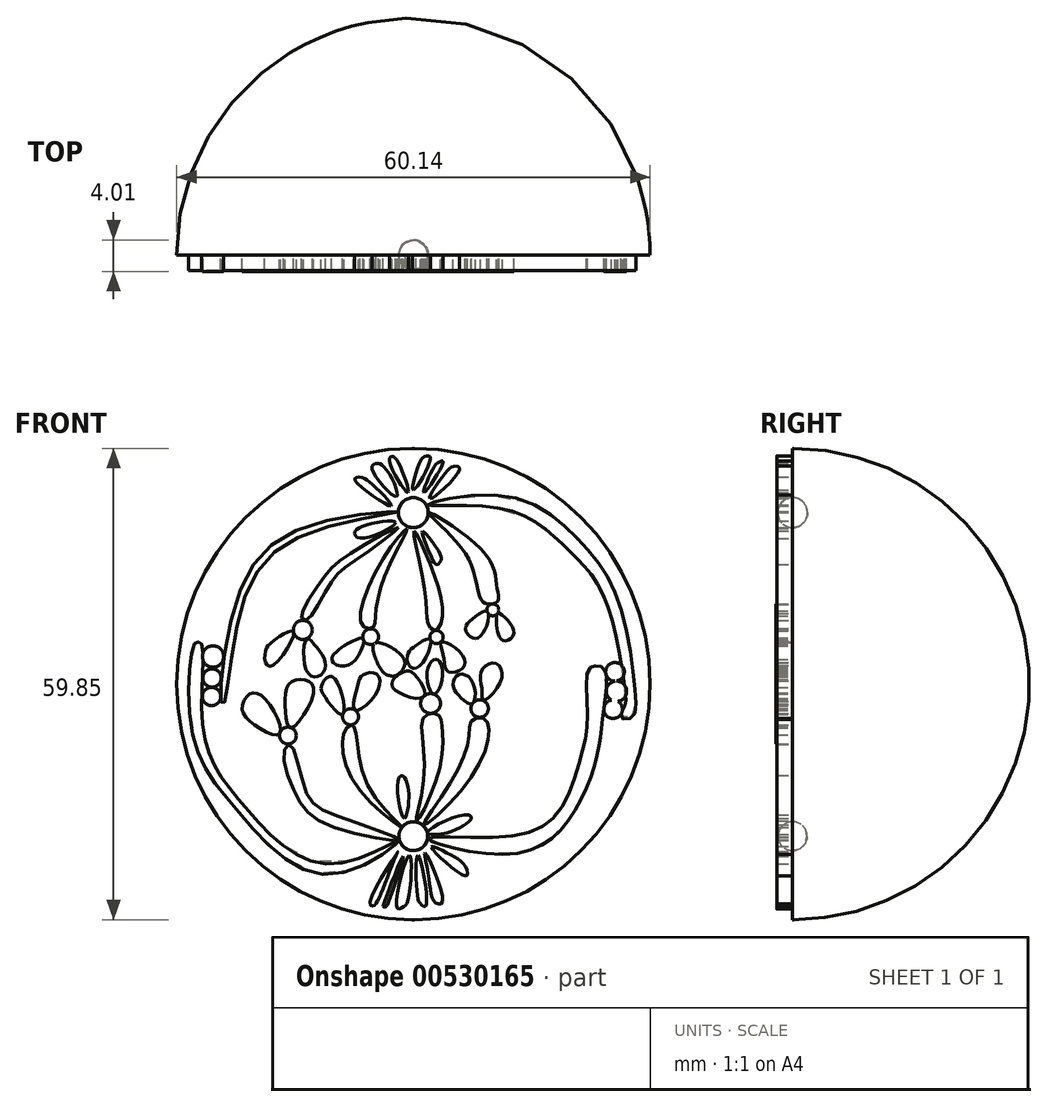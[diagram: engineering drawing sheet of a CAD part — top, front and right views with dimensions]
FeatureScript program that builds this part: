
annotation { "Feature Type Name" : "Feature", "Feature Type Description" : "" }
export const myFeature = defineFeature(function(context is Context, id is Id, definition is map)
    precondition{}
    {
        {
            var Q0;
            Q0=qCreatedBy(makeId("Front.planeOp"),FACE);
            var sketch = newSketch(context, id + "F0", { "sketchPlane" : qUnion([Q0])});
            skArc(sketch, "E0", {"start": v(0, 0) * mm, "mid": v(30.07, 29.93) * mm, "end": v(0, 59.85) * mm});
            skLineSegment(sketch, "E1", {"start": v(0, 0) * mm, "end": v(0, 59.85) * mm});
            skSolve(sketch);
        }
        {
            var Q0;
            Q0 = qSketchRegion(id + "F0", true);
            var Q1;
            Q1=sQuery(id+"F0.wireOp",EDGE,"E1");
            revolve(context, id + "F1", {"entities" : qUnion([Q0]), "axis" : qUnion([Q1]), "revolveType" : RevolveType.ONE_DIRECTION, "angle" : 180 * degree});
        }
        {
            var Q0;
            Q0=makeQuery(id+"F0.imprint","IMPRINT",FACE,{"disambiguationData":[TD([[makeQuery(id+"F0.imprint","IMPRINT",EDGE,{"derivedFrom":sQuery(id+"F0.wireOp",EDGE,"E0")}),1.0]])]});
            var sketch = newSketch(context, id + "F2", { "sketchPlane" : qUnion([Q0])});
            skArc(sketch, "E2", {"start": v(0, 49.81) * mm, "mid": v(1.9, 51.71) * mm, "end": v(0, 53.61) * mm});
            skArc(sketch, "E3", {"start": v(0, 8.77) * mm, "mid": v(1.82, 10.6) * mm, "end": v(0, 12.44) * mm});
            skLineSegment(sketch, "E4", {"start": v(0, 53.61) * mm, "end": v(0, 8.77) * mm});
            skSolve(sketch);
        }
        {
            var Q0;
            Q0 = qSketchRegion(id + "F2", true);
            var Q1;
            Q1=sQuery(id+"F0.wireOp",EDGE,"E1");
            revolve(context, id + "F3", {"entities" : qUnion([Q0]), "axis" : qUnion([Q1]), "revolveType" : RevolveType.FULL});
        }
        {
            var Q0;
            Q0=makeQuery(id+"F0.imprint","IMPRINT",FACE,{"disambiguationData":[TD([[makeQuery(id+"F0.imprint","IMPRINT",EDGE,{"derivedFrom":sQuery(id+"F0.wireOp",EDGE,"E0")}),1.0]])]});
            var sketch = newSketch(context, id + "F4", { "sketchPlane" : qUnion([Q0])});
            skFitSpline(sketch, "E5", {"points": [v(-0.7, 54.26) * mm, v(-3.02, 58.3) * mm, v(-2.66, 58.86) * mm, v(-1.63, 57.5) * mm, v(-0.7, 54.26) * mm]});
            skFitSpline(sketch, "E6", {"points": [v(0, 54.6) * mm, v(0.8, 58.05) * mm, v(1.49, 58.84) * mm, v(2.15, 58.69) * mm, v(0, 54.6) * mm]});
            skFitSpline(sketch, "E7", {"points": [v(1.34, 54.24) * mm, v(2.41, 57.14) * mm, v(3.13, 58.05) * mm, v(3.78, 58.2) * mm, v(1.34, 54.24) * mm]});
            skFitSpline(sketch, "E8", {"points": [v(2.13, 53.49) * mm, v(4.04, 56.7) * mm, v(5.23, 57.61) * mm, v(5.88, 57.23) * mm, v(2.13, 53.49) * mm]});
            skFitSpline(sketch, "E9", {"points": [v(-2.15, 53.73) * mm, v(-3.4, 57.16) * mm, v(-4.76, 57.95) * mm, v(-5.23, 57.27) * mm, v(-2.15, 53.73) * mm]});
            skFitSpline(sketch, "E10", {"points": [v(-2.83, 52.55) * mm, v(-4.86, 54.98) * mm, v(-6.7, 56.18) * mm, v(-7.45, 55.94) * mm, v(-2.83, 52.55) * mm]});
            skFitSpline(sketch, "E11", {"points": [v(-2.25, 50.44) * mm, v(-5.68, 50.24) * mm, v(-7.45, 49.15) * mm, v(-6.63, 48.45) * mm, v(-2.25, 50.44) * mm]});
            skFitSpline(sketch, "E12", {"points": [v(1.15, 49.35) * mm, v(3.26, 46.74) * mm, v(3.52, 45.68) * mm, v(3, 45.11) * mm, v(2.37, 45.92) * mm, v(1.15, 49.35) * mm]});
            skFitSpline(sketch, "E13", {"points": [v(6.93, 51.66) * mm, v(-2.97, 8.5) * mm], "startDerivative": vector(-9.9, -43.15) * mm, "endDerivative": vector(-9.9, -43.15) * mm});
            skSolve(sketch);
        }
        {
            var Q0;
            Q0 = qSketchRegion(id + "F4", true);
            extrude(context, id + "F5", {"entities" : qUnion([Q0]), "depth" : 2 * mm, "offsetDistance" : 25 * mm});
        }
        {
            var Q0;
            Q0=makeQuery(id+"F1.opRevolve","CAP_FACE",FACE,{"disambiguationData":[OSD([sQuery(id+"F0.wireOp",EDGE,"E0"),sQuery(id+"F0.wireOp",EDGE,"E1")])],"isStart":false});
            var sketch = newSketch(context, id + "F6", { "sketchPlane" : qUnion([Q0])});
            skFitSpline(sketch, "E14", {"points": [v(-0.54, 8.19) * mm, v(-0.63, 2.62) * mm, v(-1.32, 1.58) * mm, v(-2.09, 1.52) * mm, v(-0.54, 8.19) * mm]});
            skFitSpline(sketch, "E15", {"points": [v(-1.3, 8.06) * mm, v(-3.12, 2.28) * mm, v(-3.58, 1.59) * mm, v(-3.78, 1.61) * mm, v(-3.7, 2.18) * mm, v(-1.3, 8.06) * mm]});
            skFitSpline(sketch, "E16", {"points": [v(-2.2, 8.15) * mm, v(-3.71, 4.24) * mm, v(-4.63, 2.23) * mm, v(-5.09, 1.75) * mm, v(-5.53, 2.04) * mm, v(-1.96, 8.63) * mm, v(-2.2, 8.15) * mm]});
            skFitSpline(sketch, "E17", {"points": [v(0.6, 8.14) * mm, v(0.47, 3.4) * mm, v(0.94, 2) * mm, v(1.59, 1.78) * mm, v(0.6, 8.14) * mm]});
            skFitSpline(sketch, "E18", {"points": [v(1.5, 8.5) * mm, v(1.97, 5.35) * mm, v(2.66, 2.32) * mm, v(3.66, 2.2) * mm, v(1.5, 8.5) * mm]});
            skFitSpline(sketch, "E19", {"points": [v(2.3, 9.22) * mm, v(4.2, 8.5) * mm, v(6.54, 6.87) * mm, v(6.67, 5.56) * mm, v(2.3, 9.22) * mm]});
            skFitSpline(sketch, "E20", {"points": [v(1.76, 11.07) * mm, v(3.98, 10.98) * mm, v(6.6, 12.13) * mm, v(7.36, 12.94) * mm, v(6.49, 13.32) * mm, v(1.76, 11.07) * mm]});
            skFitSpline(sketch, "E21", {"points": [v(-1.15, 12.88) * mm, v(-0.63, 14.62) * mm, v(-0.7, 16.87) * mm, v(-1.32, 18.28) * mm, v(-1.97, 17.52) * mm, v(-1.15, 12.88) * mm]});
            skSolve(sketch);
        }
        {
            var Q0;
            Q0 = qSketchRegion(id + "F6", true);
            extrude(context, id + "F7", {"entities" : qUnion([Q0]), "depth" : 2 * mm, "offsetDistance" : 25 * mm});
        }
        {
            var Q0;
            Q0=makeQuery(id+"F0.imprint","IMPRINT",FACE,{"disambiguationData":[TD([[makeQuery(id+"F0.imprint","IMPRINT",EDGE,{"derivedFrom":sQuery(id+"F0.wireOp",EDGE,"E0")}),1.0]])]});
            var sketch = newSketch(context, id + "F8", { "sketchPlane" : qUnion([Q0])});
            skFitSpline(sketch, "E22", {"points": [v(-1.98, 51.8) * mm, v(-13.57, 49.94) * mm, v(-22.66, 39.92) * mm, v(-24.32, 27.37) * mm, v(-24.07, 27.46) * mm, v(-21.82, 39.68) * mm, v(-13.27, 49.16) * mm, v(-1.98, 51.8) * mm]});
            skFitSpline(sketch, "E23", {"points": [v(-1.74, 10.12) * mm, v(-10.3, 7.09) * mm, v(-21.48, 14.42) * mm, v(-26.67, 23.9) * mm, v(-26.81, 34.85) * mm, v(-27.25, 35.29) * mm, v(-27.78, 35.05) * mm, v(-28.07, 23.67) * mm, v(-22.28, 13.78) * mm, v(-10.27, 5.73) * mm, v(-1.74, 10.12) * mm]});
            skSolve(sketch);
        }
        {
            var Q0;
            Q0 = qSketchRegion(id + "F8", true);
            extrude(context, id + "F9", {"entities" : qUnion([Q0]), "depth" : 2 * mm, "offsetDistance" : 25 * mm});
        }
        {
            var Q0;
            Q0=makeQuery(id+"F1.opRevolve","CAP_FACE",FACE,{"disambiguationData":[OSD([sQuery(id+"F0.wireOp",EDGE,"E0"),sQuery(id+"F0.wireOp",EDGE,"E1")])],"isStart":false});
            var sketch = newSketch(context, id + "F10", { "sketchPlane" : qUnion([Q0])});
            skPoint(sketch, "E24.0.internal.snap0", {"position": v(-1.9, 51.71) * mm});
            skFitSpline(sketch, "E24", {"points": [v(-1.9, 49.81) * mm, v(-8.07, 46.5) * mm, v(-11.68, 43.09) * mm, v(-14.2, 38.3) * mm, v(-13.52, 38.1) * mm, v(-10.52, 42.73) * mm, v(-7.4, 45.61) * mm, v(-1.9, 49.81) * mm]});
            skFitSpline(sketch, "E25", {"points": [v(-1.76, 10.13) * mm, v(-10.35, 11.84) * mm, v(-14.8, 15.68) * mm, v(-16.41, 21.48) * mm, v(-15.63, 22.2) * mm, v(-13.68, 16.34) * mm, v(-10, 13.29) * mm, v(-1.76, 10.13) * mm]});
            skSolve(sketch);
        }
        {
            var Q0;
            Q0 = qSketchRegion(id + "F10", true);
            extrude(context, id + "F11", {"entities" : qUnion([Q0]), "depth" : 2 * mm, "offsetDistance" : 25 * mm});
        }
        {
            var Q0;
            Q0=makeQuery(id+"F1.opRevolve","CAP_FACE",FACE,{"disambiguationData":[OSD([sQuery(id+"F0.wireOp",EDGE,"E0"),sQuery(id+"F0.wireOp",EDGE,"E1")])],"isStart":false});
            var sketch = newSketch(context, id + "F12", { "sketchPlane" : qUnion([Q0])});
            skFitSpline(sketch, "E26", {"points": [v(-1.43, 11.73) * mm, v(-7.16, 16.9) * mm, v(-8.67, 24.06) * mm, v(-7.65, 24.68) * mm, v(-5.95, 17.42) * mm, v(-1.43, 11.73) * mm]});
            skFitSpline(sketch, "E27", {"points": [v(-0.8, 49.67) * mm, v(-4.32, 45.04) * mm, v(-6.49, 37.4) * mm, v(-5.14, 37.09) * mm, v(-4.83, 38.54) * mm, v(-3.22, 44.64) * mm, v(-0.8, 49.67) * mm]});
            skPoint(sketch, "E28.1.internal.snap0", {"position": v(1.4, 9.45) * mm});
            skPoint(sketch, "E28.2.internal.snap0", {"position": v(1.4, 9.45) * mm});
            skFitSpline(sketch, "E28", {"points": [v(0.4, 12.54) * mm, v(1.4, 18.97) * mm, v(1.4, 25.8) * mm, v(3.17, 26) * mm, v(3.6, 24.89) * mm, v(3.33, 19.16) * mm, v(0.4, 12.54) * mm]});
            skFitSpline(sketch, "E29", {"points": [v(0.07, 49.36) * mm, v(2.33, 44.63) * mm, v(3.7, 38.34) * mm, v(2.77, 36.75) * mm, v(1.9, 37.49) * mm, v(1.56, 41.14) * mm, v(0.07, 49.36) * mm]});
            skSolve(sketch);
        }
        {
            var Q0;
            Q0 = qSketchRegion(id + "F12", true);
            extrude(context, id + "F13", {"entities" : qUnion([Q0]), "depth" : 2 * mm, "offsetDistance" : 25 * mm});
        }
        {
            var Q0;
            Q0=makeQuery(id+"F1.opRevolve","CAP_FACE",FACE,{"disambiguationData":[OSD([sQuery(id+"F0.wireOp",EDGE,"E0"),sQuery(id+"F0.wireOp",EDGE,"E1")])],"isStart":false});
            var sketch = newSketch(context, id + "F14", { "sketchPlane" : qUnion([Q0])});
            skFitSpline(sketch, "E30", {"points": [v(1.9, 51.71) * mm, v(6.97, 45.88) * mm, v(8.88, 40.32) * mm, v(10.67, 40.4) * mm, v(10.64, 42.1) * mm, v(9.2, 46.4) * mm, v(1.9, 51.71) * mm]});
            skFitSpline(sketch, "E31", {"points": [v(1.32, 12.04) * mm, v(4.51, 17.05) * mm, v(7.1, 23.39) * mm, v(7.4, 25.28) * mm, v(9, 25.55) * mm, v(9.6, 23.4) * mm, v(6.1, 16.4) * mm, v(1.32, 12.04) * mm]});
            skSolve(sketch);
        }
        {
            var Q0;
            Q0 = qSketchRegion(id + "F14", true);
            extrude(context, id + "F15", {"entities" : qUnion([Q0]), "depth" : 2 * mm, "offsetDistance" : 25 * mm});
        }
        {
            var Q0;
            Q0=makeQuery(id+"F1.opRevolve","CAP_FACE",FACE,{"disambiguationData":[OSD([sQuery(id+"F0.wireOp",EDGE,"E0"),sQuery(id+"F0.wireOp",EDGE,"E1")])],"isStart":false});
            var sketch = newSketch(context, id + "F16", { "sketchPlane" : qUnion([Q0])});
            skFitSpline(sketch, "E32", {"points": [v(1.85, 52.7) * mm, v(11.43, 53.86) * mm, v(20.84, 48.41) * mm, v(25.86, 40.99) * mm, v(28.2, 28.78) * mm, v(27.73, 25.67) * mm, v(26.41, 25.68) * mm, v(26.81, 27.12) * mm, v(26.94, 28.61) * mm, v(24.44, 40.5) * mm, v(19.62, 47.03) * mm, v(11.21, 52.23) * mm, v(1.85, 52.7) * mm]});
            skFitSpline(sketch, "E33", {"points": [v(1.92, 10.29) * mm, v(11.74, 8.3) * mm, v(19.77, 12.68) * mm, v(23.33, 20.79) * mm, v(24.1, 26.1) * mm, v(24.28, 31.8) * mm, v(23.08, 32.26) * mm, v(22.2, 31.66) * mm, v(22.13, 26) * mm, v(21.35, 20.92) * mm, v(18.4, 13.64) * mm, v(11.44, 10.51) * mm, v(1.92, 10.29) * mm]});
            skSolve(sketch);
        }
        {
            var Q0;
            Q0 = qSketchRegion(id + "F16", true);
            extrude(context, id + "F17", {"entities" : qUnion([Q0]), "depth" : 2 * mm, "offsetDistance" : 25 * mm});
        }
        {
            var Q0;
            Q0=makeQuery(id+"F1.opRevolve","CAP_FACE",FACE,{"disambiguationData":[OSD([sQuery(id+"F0.wireOp",EDGE,"E0"),sQuery(id+"F0.wireOp",EDGE,"E1")])],"isStart":false});
            var sketch = newSketch(context, id + "F18", { "sketchPlane" : qUnion([Q0])});
            skCircle(sketch, "E34", {"center": v(-25.45, 33.43) * mm, "radius": 1.36 * mm});
            skCircle(sketch, "E35", {"center": v(-25.58, 30.7) * mm, "radius": 1.17 * mm});
            skCircle(sketch, "E36", {"center": v(-25.64, 28.35) * mm, "radius": 1.17 * mm});
            skSolve(sketch);
        }
        {
            var Q0;
            Q0 = qSketchRegion(id + "F18", true);
            extrude(context, id + "F19", {"entities" : qUnion([Q0]), "depth" : 2.1 * mm, "offsetDistance" : 25 * mm});
        }
        {
            var Q0;
            Q0=makeQuery(id+"F1.opRevolve","CAP_FACE",FACE,{"disambiguationData":[OSD([sQuery(id+"F0.wireOp",EDGE,"E0"),sQuery(id+"F0.wireOp",EDGE,"E1")])],"isStart":false});
            var sketch = newSketch(context, id + "F20", { "sketchPlane" : qUnion([Q0])});
            skCircle(sketch, "E37", {"center": v(25.38, 26.74) * mm, "radius": 1.18 * mm});
            skCircle(sketch, "E38", {"center": v(25.8, 29.01) * mm, "radius": 1.3 * mm});
            skCircle(sketch, "E39", {"center": v(25.62, 31.48) * mm, "radius": 1.19 * mm});
            skSolve(sketch);
        }
        {
            var Q0;
            Q0 = qSketchRegion(id + "F20", true);
            extrude(context, id + "F21", {"entities" : qUnion([Q0]), "depth" : 2.1 * mm, "offsetDistance" : 25 * mm});
        }
        {
            var Q0;
            {var subQ0=sQuery(id+"F0.wireOp",EDGE,"E0");Q0=makeQuery(id+"F21.boolean.opBoolean","SPLIT",FACE,{"disambiguationData":[TD([makeQuery(id+"F1.opRevolve","SWEPT_FACE",FACE,{"disambiguationData":[OSD([subQ0])]}),makeQuery(id+"F3.opRevolve","SWEPT_FACE",FACE,{"disambiguationData":[OSD([sQuery(id+"F2.wireOp",EDGE,"E2")])]}),makeQuery(id+"F3.opRevolve","SWEPT_FACE",FACE,{"disambiguationData":[OSD([sQuery(id+"F2.wireOp",EDGE,"E3")])]}),makeQuery(id+"F5.opExtrude","SWEPT_FACE",FACE,{"disambiguationData":[OSD([sQuery(id+"F4.wireOp",EDGE,"E5")])]}),makeQuery(id+"F5.opExtrude","SWEPT_FACE",FACE,{"disambiguationData":[OSD([sQuery(id+"F4.wireOp",EDGE,"E6")])]}),makeQuery(id+"F5.opExtrude","SWEPT_FACE",FACE,{"disambiguationData":[OSD([sQuery(id+"F4.wireOp",EDGE,"E7")])]}),makeQuery(id+"F5.opExtrude","SWEPT_FACE",FACE,{"disambiguationData":[OSD([sQuery(id+"F4.wireOp",EDGE,"E8")])]}),makeQuery(id+"F5.opExtrude","SWEPT_FACE",FACE,{"disambiguationData":[OSD([sQuery(id+"F4.wireOp",EDGE,"E9")])]}),makeQuery(id+"F5.opExtrude","SWEPT_FACE",FACE,{"disambiguationData":[OSD([sQuery(id+"F4.wireOp",EDGE,"E10")])]}),makeQuery(id+"F5.opExtrude","SWEPT_FACE",FACE,{"disambiguationData":[OSD([sQuery(id+"F4.wireOp",EDGE,"E11")])]}),makeQuery(id+"F5.opExtrude","SWEPT_FACE",FACE,{"disambiguationData":[OSD([sQuery(id+"F4.wireOp",EDGE,"E12")])]}),makeQuery(id+"F7.opExtrude","SWEPT_FACE",FACE,{"disambiguationData":[OSD([sQuery(id+"F6.wireOp",EDGE,"E14")])]}),makeQuery(id+"F7.opExtrude","SWEPT_FACE",FACE,{"disambiguationData":[OSD([sQuery(id+"F6.wireOp",EDGE,"E15")])]}),makeQuery(id+"F7.opExtrude","SWEPT_FACE",FACE,{"disambiguationData":[OSD([sQuery(id+"F6.wireOp",EDGE,"E16")])]}),makeQuery(id+"F7.opExtrude","SWEPT_FACE",FACE,{"disambiguationData":[OSD([sQuery(id+"F6.wireOp",EDGE,"E17")])]}),makeQuery(id+"F7.opExtrude","SWEPT_FACE",FACE,{"disambiguationData":[OSD([sQuery(id+"F6.wireOp",EDGE,"E18")])]}),makeQuery(id+"F7.opExtrude","SWEPT_FACE",FACE,{"disambiguationData":[OSD([sQuery(id+"F6.wireOp",EDGE,"E19")])]}),makeQuery(id+"F7.opExtrude","SWEPT_FACE",FACE,{"disambiguationData":[OSD([sQuery(id+"F6.wireOp",EDGE,"E20")])]}),makeQuery(id+"F7.opExtrude","SWEPT_FACE",FACE,{"disambiguationData":[OSD([sQuery(id+"F6.wireOp",EDGE,"E21")])]}),makeQuery(id+"F9.opExtrude","SWEPT_FACE",FACE,{"disambiguationData":[OSD([sQuery(id+"F8.wireOp",EDGE,"E22")])]}),makeQuery(id+"F9.opExtrude","SWEPT_FACE",FACE,{"disambiguationData":[OSD([sQuery(id+"F8.wireOp",EDGE,"E23")])]}),makeQuery(id+"F11.opExtrude","SWEPT_FACE",FACE,{"disambiguationData":[OSD([sQuery(id+"F10.wireOp",EDGE,"E24")])]}),makeQuery(id+"F11.opExtrude","SWEPT_FACE",FACE,{"disambiguationData":[OSD([sQuery(id+"F10.wireOp",EDGE,"E25")])]}),makeQuery(id+"F13.opExtrude","SWEPT_FACE",FACE,{"disambiguationData":[OSD([sQuery(id+"F12.wireOp",EDGE,"E26")])]}),makeQuery(id+"F13.opExtrude","SWEPT_FACE",FACE,{"disambiguationData":[OSD([sQuery(id+"F12.wireOp",EDGE,"E27")])]}),makeQuery(id+"F13.opExtrude","SWEPT_FACE",FACE,{"disambiguationData":[OSD([sQuery(id+"F12.wireOp",EDGE,"E28")])]}),makeQuery(id+"F13.opExtrude","SWEPT_FACE",FACE,{"disambiguationData":[OSD([sQuery(id+"F12.wireOp",EDGE,"E29")])]}),makeQuery(id+"F15.opExtrude","SWEPT_FACE",FACE,{"disambiguationData":[OSD([sQuery(id+"F14.wireOp",EDGE,"E30")])]}),makeQuery(id+"F15.opExtrude","SWEPT_FACE",FACE,{"disambiguationData":[OSD([sQuery(id+"F14.wireOp",EDGE,"E31")])]}),makeQuery(id+"F17.opExtrude","SWEPT_FACE",FACE,{"disambiguationData":[OSD([sQuery(id+"F16.wireOp",EDGE,"E32")])]}),makeQuery(id+"F17.opExtrude","SWEPT_FACE",FACE,{"disambiguationData":[OSD([sQuery(id+"F16.wireOp",EDGE,"E33")])]}),makeQuery(id+"F19.opExtrude","SWEPT_FACE",FACE,{"disambiguationData":[OSD([sQuery(id+"F18.wireOp",EDGE,"E34")])]}),makeQuery(id+"F19.opExtrude","SWEPT_FACE",FACE,{"disambiguationData":[OSD([sQuery(id+"F18.wireOp",EDGE,"E35")])]}),makeQuery(id+"F19.opExtrude","SWEPT_FACE",FACE,{"disambiguationData":[OSD([sQuery(id+"F18.wireOp",EDGE,"E36")])]}),makeQuery(id+"F21.opExtrude","SWEPT_FACE",FACE,{"disambiguationData":[OSD([sQuery(id+"F20.wireOp",EDGE,"E37")])]}),makeQuery(id+"F21.opExtrude","SWEPT_FACE",FACE,{"disambiguationData":[OSD([sQuery(id+"F20.wireOp",EDGE,"E39")])]})])],"derivedFrom":makeQuery(id+"F1.opRevolve","CAP_FACE",FACE,{"disambiguationData":[OSD([subQ0,sQuery(id+"F0.wireOp",EDGE,"E1")])],"isStart":false})});}
            var sketch = newSketch(context, id + "F22", { "sketchPlane" : qUnion([Q0])});
            skCircle(sketch, "E40", {"center": v(-14.04, 36.8) * mm, "radius": 1.2 * mm});
            skCircle(sketch, "E41", {"center": v(-15.93, 23.4) * mm, "radius": 1.07 * mm});
            skCircle(sketch, "E42", {"center": v(-5.42, 35.95) * mm, "radius": 1 * mm});
            skCircle(sketch, "E43", {"center": v(-7.99, 25.78) * mm, "radius": 1.02 * mm});
            skSolve(sketch);
        }
        {
            var Q0;
            Q0 = qSketchRegion(id + "F22", true);
            extrude(context, id + "F23", {"entities" : qUnion([Q0]), "depth" : 2.1 * mm, "offsetDistance" : 25 * mm});
        }
        {
            var Q0;
            {var subQ0=sQuery(id+"F0.wireOp",EDGE,"E0");Q0=makeQuery(id+"F21.boolean.opBoolean","SPLIT",FACE,{"disambiguationData":[TD([makeQuery(id+"F1.opRevolve","SWEPT_FACE",FACE,{"disambiguationData":[OSD([subQ0])]}),makeQuery(id+"F3.opRevolve","SWEPT_FACE",FACE,{"disambiguationData":[OSD([sQuery(id+"F2.wireOp",EDGE,"E2")])]}),makeQuery(id+"F3.opRevolve","SWEPT_FACE",FACE,{"disambiguationData":[OSD([sQuery(id+"F2.wireOp",EDGE,"E3")])]}),makeQuery(id+"F5.opExtrude","SWEPT_FACE",FACE,{"disambiguationData":[OSD([sQuery(id+"F4.wireOp",EDGE,"E5")])]}),makeQuery(id+"F5.opExtrude","SWEPT_FACE",FACE,{"disambiguationData":[OSD([sQuery(id+"F4.wireOp",EDGE,"E6")])]}),makeQuery(id+"F5.opExtrude","SWEPT_FACE",FACE,{"disambiguationData":[OSD([sQuery(id+"F4.wireOp",EDGE,"E7")])]}),makeQuery(id+"F5.opExtrude","SWEPT_FACE",FACE,{"disambiguationData":[OSD([sQuery(id+"F4.wireOp",EDGE,"E8")])]}),makeQuery(id+"F5.opExtrude","SWEPT_FACE",FACE,{"disambiguationData":[OSD([sQuery(id+"F4.wireOp",EDGE,"E9")])]}),makeQuery(id+"F5.opExtrude","SWEPT_FACE",FACE,{"disambiguationData":[OSD([sQuery(id+"F4.wireOp",EDGE,"E10")])]}),makeQuery(id+"F5.opExtrude","SWEPT_FACE",FACE,{"disambiguationData":[OSD([sQuery(id+"F4.wireOp",EDGE,"E11")])]}),makeQuery(id+"F5.opExtrude","SWEPT_FACE",FACE,{"disambiguationData":[OSD([sQuery(id+"F4.wireOp",EDGE,"E12")])]}),makeQuery(id+"F7.opExtrude","SWEPT_FACE",FACE,{"disambiguationData":[OSD([sQuery(id+"F6.wireOp",EDGE,"E14")])]}),makeQuery(id+"F7.opExtrude","SWEPT_FACE",FACE,{"disambiguationData":[OSD([sQuery(id+"F6.wireOp",EDGE,"E15")])]}),makeQuery(id+"F7.opExtrude","SWEPT_FACE",FACE,{"disambiguationData":[OSD([sQuery(id+"F6.wireOp",EDGE,"E16")])]}),makeQuery(id+"F7.opExtrude","SWEPT_FACE",FACE,{"disambiguationData":[OSD([sQuery(id+"F6.wireOp",EDGE,"E17")])]}),makeQuery(id+"F7.opExtrude","SWEPT_FACE",FACE,{"disambiguationData":[OSD([sQuery(id+"F6.wireOp",EDGE,"E18")])]}),makeQuery(id+"F7.opExtrude","SWEPT_FACE",FACE,{"disambiguationData":[OSD([sQuery(id+"F6.wireOp",EDGE,"E19")])]}),makeQuery(id+"F7.opExtrude","SWEPT_FACE",FACE,{"disambiguationData":[OSD([sQuery(id+"F6.wireOp",EDGE,"E20")])]}),makeQuery(id+"F7.opExtrude","SWEPT_FACE",FACE,{"disambiguationData":[OSD([sQuery(id+"F6.wireOp",EDGE,"E21")])]}),makeQuery(id+"F9.opExtrude","SWEPT_FACE",FACE,{"disambiguationData":[OSD([sQuery(id+"F8.wireOp",EDGE,"E22")])]}),makeQuery(id+"F9.opExtrude","SWEPT_FACE",FACE,{"disambiguationData":[OSD([sQuery(id+"F8.wireOp",EDGE,"E23")])]}),makeQuery(id+"F11.opExtrude","SWEPT_FACE",FACE,{"disambiguationData":[OSD([sQuery(id+"F10.wireOp",EDGE,"E24")])]}),makeQuery(id+"F11.opExtrude","SWEPT_FACE",FACE,{"disambiguationData":[OSD([sQuery(id+"F10.wireOp",EDGE,"E25")])]}),makeQuery(id+"F13.opExtrude","SWEPT_FACE",FACE,{"disambiguationData":[OSD([sQuery(id+"F12.wireOp",EDGE,"E26")])]}),makeQuery(id+"F13.opExtrude","SWEPT_FACE",FACE,{"disambiguationData":[OSD([sQuery(id+"F12.wireOp",EDGE,"E27")])]}),makeQuery(id+"F13.opExtrude","SWEPT_FACE",FACE,{"disambiguationData":[OSD([sQuery(id+"F12.wireOp",EDGE,"E28")])]}),makeQuery(id+"F13.opExtrude","SWEPT_FACE",FACE,{"disambiguationData":[OSD([sQuery(id+"F12.wireOp",EDGE,"E29")])]}),makeQuery(id+"F15.opExtrude","SWEPT_FACE",FACE,{"disambiguationData":[OSD([sQuery(id+"F14.wireOp",EDGE,"E30")])]}),makeQuery(id+"F15.opExtrude","SWEPT_FACE",FACE,{"disambiguationData":[OSD([sQuery(id+"F14.wireOp",EDGE,"E31")])]}),makeQuery(id+"F17.opExtrude","SWEPT_FACE",FACE,{"disambiguationData":[OSD([sQuery(id+"F16.wireOp",EDGE,"E32")])]}),makeQuery(id+"F17.opExtrude","SWEPT_FACE",FACE,{"disambiguationData":[OSD([sQuery(id+"F16.wireOp",EDGE,"E33")])]}),makeQuery(id+"F19.opExtrude","SWEPT_FACE",FACE,{"disambiguationData":[OSD([sQuery(id+"F18.wireOp",EDGE,"E34")])]}),makeQuery(id+"F19.opExtrude","SWEPT_FACE",FACE,{"disambiguationData":[OSD([sQuery(id+"F18.wireOp",EDGE,"E35")])]}),makeQuery(id+"F19.opExtrude","SWEPT_FACE",FACE,{"disambiguationData":[OSD([sQuery(id+"F18.wireOp",EDGE,"E36")])]}),makeQuery(id+"F21.opExtrude","SWEPT_FACE",FACE,{"disambiguationData":[OSD([sQuery(id+"F20.wireOp",EDGE,"E37")])]}),makeQuery(id+"F21.opExtrude","SWEPT_FACE",FACE,{"disambiguationData":[OSD([sQuery(id+"F20.wireOp",EDGE,"E39")])]})])],"derivedFrom":makeQuery(id+"F1.opRevolve","CAP_FACE",FACE,{"disambiguationData":[OSD([subQ0,sQuery(id+"F0.wireOp",EDGE,"E1")])],"isStart":false})});}
            var sketch = newSketch(context, id + "F24", { "sketchPlane" : qUnion([Q0])});
            skCircle(sketch, "E44", {"center": v(2.94, 35.9) * mm, "radius": 0.84 * mm});
            skCircle(sketch, "E45", {"center": v(2.18, 27.46) * mm, "radius": 1.26 * mm});
            skCircle(sketch, "E46", {"center": v(10.1, 39.35) * mm, "radius": 0.75 * mm});
            skCircle(sketch, "E47", {"center": v(8.42, 26.82) * mm, "radius": 1.11 * mm});
            skSolve(sketch);
        }
        {
            var Q0;
            Q0 = qSketchRegion(id + "F24", true);
            extrude(context, id + "F25", {"entities" : qUnion([Q0]), "depth" : 2.1 * mm, "offsetDistance" : 25 * mm});
        }
        {
            var Q0;
            {var subQ0=sQuery(id+"F0.wireOp",EDGE,"E0");Q0=makeQuery(id+"F21.boolean.opBoolean","SPLIT",FACE,{"disambiguationData":[TD([makeQuery(id+"F1.opRevolve","SWEPT_FACE",FACE,{"disambiguationData":[OSD([subQ0])]}),makeQuery(id+"F5.opExtrude","SWEPT_FACE",FACE,{"disambiguationData":[OSD([sQuery(id+"F4.wireOp",EDGE,"E5")])]}),makeQuery(id+"F5.opExtrude","SWEPT_FACE",FACE,{"disambiguationData":[OSD([sQuery(id+"F4.wireOp",EDGE,"E6")])]}),makeQuery(id+"F5.opExtrude","SWEPT_FACE",FACE,{"disambiguationData":[OSD([sQuery(id+"F4.wireOp",EDGE,"E7")])]}),makeQuery(id+"F5.opExtrude","SWEPT_FACE",FACE,{"disambiguationData":[OSD([sQuery(id+"F4.wireOp",EDGE,"E8")])]}),makeQuery(id+"F5.opExtrude","SWEPT_FACE",FACE,{"disambiguationData":[OSD([sQuery(id+"F4.wireOp",EDGE,"E9")])]}),makeQuery(id+"F5.opExtrude","SWEPT_FACE",FACE,{"disambiguationData":[OSD([sQuery(id+"F4.wireOp",EDGE,"E10")])]}),makeQuery(id+"F5.opExtrude","SWEPT_FACE",FACE,{"disambiguationData":[OSD([sQuery(id+"F4.wireOp",EDGE,"E11")])]}),makeQuery(id+"F5.opExtrude","SWEPT_FACE",FACE,{"disambiguationData":[OSD([sQuery(id+"F4.wireOp",EDGE,"E12")])]}),makeQuery(id+"F7.opExtrude","SWEPT_FACE",FACE,{"disambiguationData":[OSD([sQuery(id+"F6.wireOp",EDGE,"E14")])]}),makeQuery(id+"F7.opExtrude","SWEPT_FACE",FACE,{"disambiguationData":[OSD([sQuery(id+"F6.wireOp",EDGE,"E15")])]}),makeQuery(id+"F7.opExtrude","SWEPT_FACE",FACE,{"disambiguationData":[OSD([sQuery(id+"F6.wireOp",EDGE,"E16")])]}),makeQuery(id+"F7.opExtrude","SWEPT_FACE",FACE,{"disambiguationData":[OSD([sQuery(id+"F6.wireOp",EDGE,"E17")])]}),makeQuery(id+"F7.opExtrude","SWEPT_FACE",FACE,{"disambiguationData":[OSD([sQuery(id+"F6.wireOp",EDGE,"E18")])]}),makeQuery(id+"F7.opExtrude","SWEPT_FACE",FACE,{"disambiguationData":[OSD([sQuery(id+"F6.wireOp",EDGE,"E19")])]}),makeQuery(id+"F7.opExtrude","SWEPT_FACE",FACE,{"disambiguationData":[OSD([sQuery(id+"F6.wireOp",EDGE,"E20")])]}),makeQuery(id+"F7.opExtrude","SWEPT_FACE",FACE,{"disambiguationData":[OSD([sQuery(id+"F6.wireOp",EDGE,"E21")])]}),makeQuery(id+"F9.opExtrude","SWEPT_FACE",FACE,{"disambiguationData":[OSD([sQuery(id+"F8.wireOp",EDGE,"E22")])]}),makeQuery(id+"F9.opExtrude","SWEPT_FACE",FACE,{"disambiguationData":[OSD([sQuery(id+"F8.wireOp",EDGE,"E23")])]}),makeQuery(id+"F11.opExtrude","SWEPT_FACE",FACE,{"disambiguationData":[OSD([sQuery(id+"F10.wireOp",EDGE,"E24")])]}),makeQuery(id+"F11.opExtrude","SWEPT_FACE",FACE,{"disambiguationData":[OSD([sQuery(id+"F10.wireOp",EDGE,"E25")])]}),makeQuery(id+"F13.opExtrude","SWEPT_FACE",FACE,{"disambiguationData":[OSD([sQuery(id+"F12.wireOp",EDGE,"E26")])]}),makeQuery(id+"F13.opExtrude","SWEPT_FACE",FACE,{"disambiguationData":[OSD([sQuery(id+"F12.wireOp",EDGE,"E27")])]}),makeQuery(id+"F13.opExtrude","SWEPT_FACE",FACE,{"disambiguationData":[OSD([sQuery(id+"F12.wireOp",EDGE,"E28")])]}),makeQuery(id+"F13.opExtrude","SWEPT_FACE",FACE,{"disambiguationData":[OSD([sQuery(id+"F12.wireOp",EDGE,"E29")])]}),makeQuery(id+"F15.opExtrude","SWEPT_FACE",FACE,{"disambiguationData":[OSD([sQuery(id+"F14.wireOp",EDGE,"E30")])]}),makeQuery(id+"F15.opExtrude","SWEPT_FACE",FACE,{"disambiguationData":[OSD([sQuery(id+"F14.wireOp",EDGE,"E31")])]}),makeQuery(id+"F17.opExtrude","SWEPT_FACE",FACE,{"disambiguationData":[OSD([sQuery(id+"F16.wireOp",EDGE,"E32")])]}),makeQuery(id+"F17.opExtrude","SWEPT_FACE",FACE,{"disambiguationData":[OSD([sQuery(id+"F16.wireOp",EDGE,"E33")])]}),makeQuery(id+"F19.opExtrude","SWEPT_FACE",FACE,{"disambiguationData":[OSD([sQuery(id+"F18.wireOp",EDGE,"E34")])]}),makeQuery(id+"F19.opExtrude","SWEPT_FACE",FACE,{"disambiguationData":[OSD([sQuery(id+"F18.wireOp",EDGE,"E35")])]}),makeQuery(id+"F19.opExtrude","SWEPT_FACE",FACE,{"disambiguationData":[OSD([sQuery(id+"F18.wireOp",EDGE,"E36")])]}),makeQuery(id+"F21.opExtrude","SWEPT_FACE",FACE,{"disambiguationData":[OSD([sQuery(id+"F20.wireOp",EDGE,"E37")])]}),makeQuery(id+"F21.opExtrude","SWEPT_FACE",FACE,{"disambiguationData":[OSD([sQuery(id+"F20.wireOp",EDGE,"E39")])]})])],"derivedFrom":makeQuery(id+"F1.opRevolve","CAP_FACE",FACE,{"disambiguationData":[OSD([subQ0,sQuery(id+"F0.wireOp",EDGE,"E1")])],"isStart":false})});}
            var sketch = newSketch(context, id + "F26", { "sketchPlane" : qUnion([Q0])});
            skFitSpline(sketch, "E48", {"points": [v(-15.22, 36.53) * mm, v(-16.83, 36.06) * mm, v(-18.04, 35.18) * mm, v(-18.6, 34.57) * mm, v(-18.84, 32.93) * mm, v(-17.98, 32.22) * mm, v(-15.22, 36.53) * mm]});
            skFitSpline(sketch, "E49", {"points": [v(-13.52, 35.72) * mm, v(-12.57, 34.95) * mm, v(-11.32, 33.17) * mm, v(-11.32, 31.57) * mm, v(-12.6, 30.84) * mm, v(-13.8, 32.3) * mm, v(-13.52, 35.72) * mm]});
            skSolve(sketch);
        }
        {
            var Q0;
            Q0 = qSketchRegion(id + "F26", true);
            extrude(context, id + "F27", {"entities" : qUnion([Q0]), "depth" : 2.1 * mm, "offsetDistance" : 25 * mm});
        }
        {
            var Q0;
            {var subQ0=sQuery(id+"F0.wireOp",EDGE,"E0");Q0=makeQuery(id+"F21.boolean.opBoolean","SPLIT",FACE,{"disambiguationData":[TD([makeQuery(id+"F1.opRevolve","SWEPT_FACE",FACE,{"disambiguationData":[OSD([subQ0])]}),makeQuery(id+"F5.opExtrude","SWEPT_FACE",FACE,{"disambiguationData":[OSD([sQuery(id+"F4.wireOp",EDGE,"E5")])]}),makeQuery(id+"F5.opExtrude","SWEPT_FACE",FACE,{"disambiguationData":[OSD([sQuery(id+"F4.wireOp",EDGE,"E6")])]}),makeQuery(id+"F5.opExtrude","SWEPT_FACE",FACE,{"disambiguationData":[OSD([sQuery(id+"F4.wireOp",EDGE,"E7")])]}),makeQuery(id+"F5.opExtrude","SWEPT_FACE",FACE,{"disambiguationData":[OSD([sQuery(id+"F4.wireOp",EDGE,"E8")])]}),makeQuery(id+"F5.opExtrude","SWEPT_FACE",FACE,{"disambiguationData":[OSD([sQuery(id+"F4.wireOp",EDGE,"E9")])]}),makeQuery(id+"F5.opExtrude","SWEPT_FACE",FACE,{"disambiguationData":[OSD([sQuery(id+"F4.wireOp",EDGE,"E10")])]}),makeQuery(id+"F5.opExtrude","SWEPT_FACE",FACE,{"disambiguationData":[OSD([sQuery(id+"F4.wireOp",EDGE,"E11")])]}),makeQuery(id+"F5.opExtrude","SWEPT_FACE",FACE,{"disambiguationData":[OSD([sQuery(id+"F4.wireOp",EDGE,"E12")])]}),makeQuery(id+"F7.opExtrude","SWEPT_FACE",FACE,{"disambiguationData":[OSD([sQuery(id+"F6.wireOp",EDGE,"E14")])]}),makeQuery(id+"F7.opExtrude","SWEPT_FACE",FACE,{"disambiguationData":[OSD([sQuery(id+"F6.wireOp",EDGE,"E15")])]}),makeQuery(id+"F7.opExtrude","SWEPT_FACE",FACE,{"disambiguationData":[OSD([sQuery(id+"F6.wireOp",EDGE,"E16")])]}),makeQuery(id+"F7.opExtrude","SWEPT_FACE",FACE,{"disambiguationData":[OSD([sQuery(id+"F6.wireOp",EDGE,"E17")])]}),makeQuery(id+"F7.opExtrude","SWEPT_FACE",FACE,{"disambiguationData":[OSD([sQuery(id+"F6.wireOp",EDGE,"E18")])]}),makeQuery(id+"F7.opExtrude","SWEPT_FACE",FACE,{"disambiguationData":[OSD([sQuery(id+"F6.wireOp",EDGE,"E19")])]}),makeQuery(id+"F7.opExtrude","SWEPT_FACE",FACE,{"disambiguationData":[OSD([sQuery(id+"F6.wireOp",EDGE,"E20")])]}),makeQuery(id+"F7.opExtrude","SWEPT_FACE",FACE,{"disambiguationData":[OSD([sQuery(id+"F6.wireOp",EDGE,"E21")])]}),makeQuery(id+"F9.opExtrude","SWEPT_FACE",FACE,{"disambiguationData":[OSD([sQuery(id+"F8.wireOp",EDGE,"E22")])]}),makeQuery(id+"F9.opExtrude","SWEPT_FACE",FACE,{"disambiguationData":[OSD([sQuery(id+"F8.wireOp",EDGE,"E23")])]}),makeQuery(id+"F11.opExtrude","SWEPT_FACE",FACE,{"disambiguationData":[OSD([sQuery(id+"F10.wireOp",EDGE,"E24")])]}),makeQuery(id+"F11.opExtrude","SWEPT_FACE",FACE,{"disambiguationData":[OSD([sQuery(id+"F10.wireOp",EDGE,"E25")])]}),makeQuery(id+"F13.opExtrude","SWEPT_FACE",FACE,{"disambiguationData":[OSD([sQuery(id+"F12.wireOp",EDGE,"E26")])]}),makeQuery(id+"F13.opExtrude","SWEPT_FACE",FACE,{"disambiguationData":[OSD([sQuery(id+"F12.wireOp",EDGE,"E27")])]}),makeQuery(id+"F13.opExtrude","SWEPT_FACE",FACE,{"disambiguationData":[OSD([sQuery(id+"F12.wireOp",EDGE,"E28")])]}),makeQuery(id+"F13.opExtrude","SWEPT_FACE",FACE,{"disambiguationData":[OSD([sQuery(id+"F12.wireOp",EDGE,"E29")])]}),makeQuery(id+"F15.opExtrude","SWEPT_FACE",FACE,{"disambiguationData":[OSD([sQuery(id+"F14.wireOp",EDGE,"E30")])]}),makeQuery(id+"F15.opExtrude","SWEPT_FACE",FACE,{"disambiguationData":[OSD([sQuery(id+"F14.wireOp",EDGE,"E31")])]}),makeQuery(id+"F17.opExtrude","SWEPT_FACE",FACE,{"disambiguationData":[OSD([sQuery(id+"F16.wireOp",EDGE,"E32")])]}),makeQuery(id+"F17.opExtrude","SWEPT_FACE",FACE,{"disambiguationData":[OSD([sQuery(id+"F16.wireOp",EDGE,"E33")])]}),makeQuery(id+"F19.opExtrude","SWEPT_FACE",FACE,{"disambiguationData":[OSD([sQuery(id+"F18.wireOp",EDGE,"E34")])]}),makeQuery(id+"F19.opExtrude","SWEPT_FACE",FACE,{"disambiguationData":[OSD([sQuery(id+"F18.wireOp",EDGE,"E35")])]}),makeQuery(id+"F19.opExtrude","SWEPT_FACE",FACE,{"disambiguationData":[OSD([sQuery(id+"F18.wireOp",EDGE,"E36")])]}),makeQuery(id+"F21.opExtrude","SWEPT_FACE",FACE,{"disambiguationData":[OSD([sQuery(id+"F20.wireOp",EDGE,"E37")])]}),makeQuery(id+"F21.opExtrude","SWEPT_FACE",FACE,{"disambiguationData":[OSD([sQuery(id+"F20.wireOp",EDGE,"E39")])]})])],"derivedFrom":makeQuery(id+"F1.opRevolve","CAP_FACE",FACE,{"disambiguationData":[OSD([subQ0,sQuery(id+"F0.wireOp",EDGE,"E1")])],"isStart":false})});}
            var sketch = newSketch(context, id + "F28", { "sketchPlane" : qUnion([Q0])});
            skFitSpline(sketch, "E50", {"points": [v(-16.98, 23.6) * mm, v(-20.1, 24.69) * mm, v(-21.75, 26.9) * mm, v(-20.7, 28.72) * mm, v(-18.56, 27.75) * mm, v(-16.98, 23.6) * mm]});
            skFitSpline(sketch, "E51", {"points": [v(-15.52, 24.38) * mm, v(-16.21, 26.35) * mm, v(-15.83, 29.89) * mm, v(-13.78, 30.47) * mm, v(-12.67, 28.93) * mm, v(-15.52, 24.38) * mm]});
            skSolve(sketch);
        }
        {
            var Q0;
            Q0 = qSketchRegion(id + "F28", true);
            extrude(context, id + "F29", {"entities" : qUnion([Q0]), "depth" : 2.1 * mm, "offsetDistance" : 25 * mm});
        }
        {
            var Q0;
            {var subQ0=sQuery(id+"F0.wireOp",EDGE,"E0");Q0=makeQuery(id+"F21.boolean.opBoolean","SPLIT",FACE,{"disambiguationData":[TD([makeQuery(id+"F1.opRevolve","SWEPT_FACE",FACE,{"disambiguationData":[OSD([subQ0])]}),makeQuery(id+"F5.opExtrude","SWEPT_FACE",FACE,{"disambiguationData":[OSD([sQuery(id+"F4.wireOp",EDGE,"E5")])]}),makeQuery(id+"F5.opExtrude","SWEPT_FACE",FACE,{"disambiguationData":[OSD([sQuery(id+"F4.wireOp",EDGE,"E6")])]}),makeQuery(id+"F5.opExtrude","SWEPT_FACE",FACE,{"disambiguationData":[OSD([sQuery(id+"F4.wireOp",EDGE,"E7")])]}),makeQuery(id+"F5.opExtrude","SWEPT_FACE",FACE,{"disambiguationData":[OSD([sQuery(id+"F4.wireOp",EDGE,"E8")])]}),makeQuery(id+"F5.opExtrude","SWEPT_FACE",FACE,{"disambiguationData":[OSD([sQuery(id+"F4.wireOp",EDGE,"E9")])]}),makeQuery(id+"F5.opExtrude","SWEPT_FACE",FACE,{"disambiguationData":[OSD([sQuery(id+"F4.wireOp",EDGE,"E10")])]}),makeQuery(id+"F5.opExtrude","SWEPT_FACE",FACE,{"disambiguationData":[OSD([sQuery(id+"F4.wireOp",EDGE,"E11")])]}),makeQuery(id+"F5.opExtrude","SWEPT_FACE",FACE,{"disambiguationData":[OSD([sQuery(id+"F4.wireOp",EDGE,"E12")])]}),makeQuery(id+"F7.opExtrude","SWEPT_FACE",FACE,{"disambiguationData":[OSD([sQuery(id+"F6.wireOp",EDGE,"E14")])]}),makeQuery(id+"F7.opExtrude","SWEPT_FACE",FACE,{"disambiguationData":[OSD([sQuery(id+"F6.wireOp",EDGE,"E15")])]}),makeQuery(id+"F7.opExtrude","SWEPT_FACE",FACE,{"disambiguationData":[OSD([sQuery(id+"F6.wireOp",EDGE,"E16")])]}),makeQuery(id+"F7.opExtrude","SWEPT_FACE",FACE,{"disambiguationData":[OSD([sQuery(id+"F6.wireOp",EDGE,"E17")])]}),makeQuery(id+"F7.opExtrude","SWEPT_FACE",FACE,{"disambiguationData":[OSD([sQuery(id+"F6.wireOp",EDGE,"E18")])]}),makeQuery(id+"F7.opExtrude","SWEPT_FACE",FACE,{"disambiguationData":[OSD([sQuery(id+"F6.wireOp",EDGE,"E19")])]}),makeQuery(id+"F7.opExtrude","SWEPT_FACE",FACE,{"disambiguationData":[OSD([sQuery(id+"F6.wireOp",EDGE,"E20")])]}),makeQuery(id+"F7.opExtrude","SWEPT_FACE",FACE,{"disambiguationData":[OSD([sQuery(id+"F6.wireOp",EDGE,"E21")])]}),makeQuery(id+"F9.opExtrude","SWEPT_FACE",FACE,{"disambiguationData":[OSD([sQuery(id+"F8.wireOp",EDGE,"E22")])]}),makeQuery(id+"F9.opExtrude","SWEPT_FACE",FACE,{"disambiguationData":[OSD([sQuery(id+"F8.wireOp",EDGE,"E23")])]}),makeQuery(id+"F11.opExtrude","SWEPT_FACE",FACE,{"disambiguationData":[OSD([sQuery(id+"F10.wireOp",EDGE,"E24")])]}),makeQuery(id+"F11.opExtrude","SWEPT_FACE",FACE,{"disambiguationData":[OSD([sQuery(id+"F10.wireOp",EDGE,"E25")])]}),makeQuery(id+"F13.opExtrude","SWEPT_FACE",FACE,{"disambiguationData":[OSD([sQuery(id+"F12.wireOp",EDGE,"E26")])]}),makeQuery(id+"F13.opExtrude","SWEPT_FACE",FACE,{"disambiguationData":[OSD([sQuery(id+"F12.wireOp",EDGE,"E27")])]}),makeQuery(id+"F13.opExtrude","SWEPT_FACE",FACE,{"disambiguationData":[OSD([sQuery(id+"F12.wireOp",EDGE,"E28")])]}),makeQuery(id+"F13.opExtrude","SWEPT_FACE",FACE,{"disambiguationData":[OSD([sQuery(id+"F12.wireOp",EDGE,"E29")])]}),makeQuery(id+"F15.opExtrude","SWEPT_FACE",FACE,{"disambiguationData":[OSD([sQuery(id+"F14.wireOp",EDGE,"E30")])]}),makeQuery(id+"F15.opExtrude","SWEPT_FACE",FACE,{"disambiguationData":[OSD([sQuery(id+"F14.wireOp",EDGE,"E31")])]}),makeQuery(id+"F17.opExtrude","SWEPT_FACE",FACE,{"disambiguationData":[OSD([sQuery(id+"F16.wireOp",EDGE,"E32")])]}),makeQuery(id+"F17.opExtrude","SWEPT_FACE",FACE,{"disambiguationData":[OSD([sQuery(id+"F16.wireOp",EDGE,"E33")])]}),makeQuery(id+"F19.opExtrude","SWEPT_FACE",FACE,{"disambiguationData":[OSD([sQuery(id+"F18.wireOp",EDGE,"E34")])]}),makeQuery(id+"F19.opExtrude","SWEPT_FACE",FACE,{"disambiguationData":[OSD([sQuery(id+"F18.wireOp",EDGE,"E35")])]}),makeQuery(id+"F19.opExtrude","SWEPT_FACE",FACE,{"disambiguationData":[OSD([sQuery(id+"F18.wireOp",EDGE,"E36")])]}),makeQuery(id+"F21.opExtrude","SWEPT_FACE",FACE,{"disambiguationData":[OSD([sQuery(id+"F20.wireOp",EDGE,"E37")])]}),makeQuery(id+"F21.opExtrude","SWEPT_FACE",FACE,{"disambiguationData":[OSD([sQuery(id+"F20.wireOp",EDGE,"E39")])]})])],"derivedFrom":makeQuery(id+"F1.opRevolve","CAP_FACE",FACE,{"disambiguationData":[OSD([subQ0,sQuery(id+"F0.wireOp",EDGE,"E1")])],"isStart":false})});}
            var sketch = newSketch(context, id + "F30", { "sketchPlane" : qUnion([Q0])});
            skFitSpline(sketch, "E52", {"points": [v(-8.94, 26.15) * mm, v(-11.25, 28.33) * mm, v(-11.6, 29.96) * mm, v(-10.2, 30.83) * mm, v(-8.94, 26.15) * mm]});
            skFitSpline(sketch, "E53", {"points": [v(-7.43, 26.63) * mm, v(-7.05, 29.89) * mm, v(-6.41, 31.09) * mm, v(-4.73, 31.24) * mm, v(-4.56, 29.01) * mm, v(-7.43, 26.63) * mm]});
            skSolve(sketch);
        }
        {
            var Q0;
            Q0 = qSketchRegion(id + "F30", true);
            extrude(context, id + "F31", {"entities" : qUnion([Q0]), "depth" : 2.1 * mm, "offsetDistance" : 25 * mm});
        }
        {
            var Q0;
            {var subQ0=sQuery(id+"F0.wireOp",EDGE,"E0");Q0=makeQuery(id+"F21.boolean.opBoolean","SPLIT",FACE,{"disambiguationData":[TD([makeQuery(id+"F1.opRevolve","SWEPT_FACE",FACE,{"disambiguationData":[OSD([subQ0])]}),makeQuery(id+"F5.opExtrude","SWEPT_FACE",FACE,{"disambiguationData":[OSD([sQuery(id+"F4.wireOp",EDGE,"E5")])]}),makeQuery(id+"F5.opExtrude","SWEPT_FACE",FACE,{"disambiguationData":[OSD([sQuery(id+"F4.wireOp",EDGE,"E6")])]}),makeQuery(id+"F5.opExtrude","SWEPT_FACE",FACE,{"disambiguationData":[OSD([sQuery(id+"F4.wireOp",EDGE,"E7")])]}),makeQuery(id+"F5.opExtrude","SWEPT_FACE",FACE,{"disambiguationData":[OSD([sQuery(id+"F4.wireOp",EDGE,"E8")])]}),makeQuery(id+"F5.opExtrude","SWEPT_FACE",FACE,{"disambiguationData":[OSD([sQuery(id+"F4.wireOp",EDGE,"E9")])]}),makeQuery(id+"F5.opExtrude","SWEPT_FACE",FACE,{"disambiguationData":[OSD([sQuery(id+"F4.wireOp",EDGE,"E10")])]}),makeQuery(id+"F5.opExtrude","SWEPT_FACE",FACE,{"disambiguationData":[OSD([sQuery(id+"F4.wireOp",EDGE,"E11")])]}),makeQuery(id+"F5.opExtrude","SWEPT_FACE",FACE,{"disambiguationData":[OSD([sQuery(id+"F4.wireOp",EDGE,"E12")])]}),makeQuery(id+"F7.opExtrude","SWEPT_FACE",FACE,{"disambiguationData":[OSD([sQuery(id+"F6.wireOp",EDGE,"E14")])]}),makeQuery(id+"F7.opExtrude","SWEPT_FACE",FACE,{"disambiguationData":[OSD([sQuery(id+"F6.wireOp",EDGE,"E15")])]}),makeQuery(id+"F7.opExtrude","SWEPT_FACE",FACE,{"disambiguationData":[OSD([sQuery(id+"F6.wireOp",EDGE,"E16")])]}),makeQuery(id+"F7.opExtrude","SWEPT_FACE",FACE,{"disambiguationData":[OSD([sQuery(id+"F6.wireOp",EDGE,"E17")])]}),makeQuery(id+"F7.opExtrude","SWEPT_FACE",FACE,{"disambiguationData":[OSD([sQuery(id+"F6.wireOp",EDGE,"E18")])]}),makeQuery(id+"F7.opExtrude","SWEPT_FACE",FACE,{"disambiguationData":[OSD([sQuery(id+"F6.wireOp",EDGE,"E19")])]}),makeQuery(id+"F7.opExtrude","SWEPT_FACE",FACE,{"disambiguationData":[OSD([sQuery(id+"F6.wireOp",EDGE,"E20")])]}),makeQuery(id+"F7.opExtrude","SWEPT_FACE",FACE,{"disambiguationData":[OSD([sQuery(id+"F6.wireOp",EDGE,"E21")])]}),makeQuery(id+"F9.opExtrude","SWEPT_FACE",FACE,{"disambiguationData":[OSD([sQuery(id+"F8.wireOp",EDGE,"E22")])]}),makeQuery(id+"F9.opExtrude","SWEPT_FACE",FACE,{"disambiguationData":[OSD([sQuery(id+"F8.wireOp",EDGE,"E23")])]}),makeQuery(id+"F11.opExtrude","SWEPT_FACE",FACE,{"disambiguationData":[OSD([sQuery(id+"F10.wireOp",EDGE,"E24")])]}),makeQuery(id+"F11.opExtrude","SWEPT_FACE",FACE,{"disambiguationData":[OSD([sQuery(id+"F10.wireOp",EDGE,"E25")])]}),makeQuery(id+"F13.opExtrude","SWEPT_FACE",FACE,{"disambiguationData":[OSD([sQuery(id+"F12.wireOp",EDGE,"E26")])]}),makeQuery(id+"F13.opExtrude","SWEPT_FACE",FACE,{"disambiguationData":[OSD([sQuery(id+"F12.wireOp",EDGE,"E27")])]}),makeQuery(id+"F13.opExtrude","SWEPT_FACE",FACE,{"disambiguationData":[OSD([sQuery(id+"F12.wireOp",EDGE,"E28")])]}),makeQuery(id+"F13.opExtrude","SWEPT_FACE",FACE,{"disambiguationData":[OSD([sQuery(id+"F12.wireOp",EDGE,"E29")])]}),makeQuery(id+"F15.opExtrude","SWEPT_FACE",FACE,{"disambiguationData":[OSD([sQuery(id+"F14.wireOp",EDGE,"E30")])]}),makeQuery(id+"F15.opExtrude","SWEPT_FACE",FACE,{"disambiguationData":[OSD([sQuery(id+"F14.wireOp",EDGE,"E31")])]}),makeQuery(id+"F17.opExtrude","SWEPT_FACE",FACE,{"disambiguationData":[OSD([sQuery(id+"F16.wireOp",EDGE,"E32")])]}),makeQuery(id+"F17.opExtrude","SWEPT_FACE",FACE,{"disambiguationData":[OSD([sQuery(id+"F16.wireOp",EDGE,"E33")])]}),makeQuery(id+"F19.opExtrude","SWEPT_FACE",FACE,{"disambiguationData":[OSD([sQuery(id+"F18.wireOp",EDGE,"E34")])]}),makeQuery(id+"F19.opExtrude","SWEPT_FACE",FACE,{"disambiguationData":[OSD([sQuery(id+"F18.wireOp",EDGE,"E35")])]}),makeQuery(id+"F19.opExtrude","SWEPT_FACE",FACE,{"disambiguationData":[OSD([sQuery(id+"F18.wireOp",EDGE,"E36")])]}),makeQuery(id+"F21.opExtrude","SWEPT_FACE",FACE,{"disambiguationData":[OSD([sQuery(id+"F20.wireOp",EDGE,"E37")])]}),makeQuery(id+"F21.opExtrude","SWEPT_FACE",FACE,{"disambiguationData":[OSD([sQuery(id+"F20.wireOp",EDGE,"E39")])]})])],"derivedFrom":makeQuery(id+"F1.opRevolve","CAP_FACE",FACE,{"disambiguationData":[OSD([subQ0,sQuery(id+"F0.wireOp",EDGE,"E1")])],"isStart":false})});}
            var sketch = newSketch(context, id + "F32", { "sketchPlane" : qUnion([Q0])});
            skFitSpline(sketch, "E54", {"points": [v(-6.4, 35.69) * mm, v(-8.3, 35.06) * mm, v(-9.64, 34.17) * mm, v(-10.36, 32.95) * mm, v(-9.04, 32.23) * mm, v(-7.17, 33.25) * mm, v(-6.4, 35.69) * mm]});
            skFitSpline(sketch, "E55", {"points": [v(-4.84, 35.14) * mm, v(-4.7, 33.56) * mm, v(-3.87, 32.12) * mm, v(-2.7, 30.92) * mm, v(-1.2, 32.14) * mm, v(-2.55, 33.93) * mm, v(-4.84, 35.14) * mm]});
            skSolve(sketch);
        }
        {
            var Q0;
            Q0 = qSketchRegion(id + "F32", true);
            extrude(context, id + "F33", {"entities" : qUnion([Q0]), "depth" : 2.1 * mm, "offsetDistance" : 25 * mm});
        }
        {
            var Q0;
            {var subQ0=sQuery(id+"F0.wireOp",EDGE,"E0");Q0=makeQuery(id+"F21.boolean.opBoolean","SPLIT",FACE,{"disambiguationData":[TD([makeQuery(id+"F1.opRevolve","SWEPT_FACE",FACE,{"disambiguationData":[OSD([subQ0])]}),makeQuery(id+"F5.opExtrude","SWEPT_FACE",FACE,{"disambiguationData":[OSD([sQuery(id+"F4.wireOp",EDGE,"E5")])]}),makeQuery(id+"F5.opExtrude","SWEPT_FACE",FACE,{"disambiguationData":[OSD([sQuery(id+"F4.wireOp",EDGE,"E6")])]}),makeQuery(id+"F5.opExtrude","SWEPT_FACE",FACE,{"disambiguationData":[OSD([sQuery(id+"F4.wireOp",EDGE,"E7")])]}),makeQuery(id+"F5.opExtrude","SWEPT_FACE",FACE,{"disambiguationData":[OSD([sQuery(id+"F4.wireOp",EDGE,"E8")])]}),makeQuery(id+"F5.opExtrude","SWEPT_FACE",FACE,{"disambiguationData":[OSD([sQuery(id+"F4.wireOp",EDGE,"E9")])]}),makeQuery(id+"F5.opExtrude","SWEPT_FACE",FACE,{"disambiguationData":[OSD([sQuery(id+"F4.wireOp",EDGE,"E10")])]}),makeQuery(id+"F5.opExtrude","SWEPT_FACE",FACE,{"disambiguationData":[OSD([sQuery(id+"F4.wireOp",EDGE,"E11")])]}),makeQuery(id+"F5.opExtrude","SWEPT_FACE",FACE,{"disambiguationData":[OSD([sQuery(id+"F4.wireOp",EDGE,"E12")])]}),makeQuery(id+"F7.opExtrude","SWEPT_FACE",FACE,{"disambiguationData":[OSD([sQuery(id+"F6.wireOp",EDGE,"E14")])]}),makeQuery(id+"F7.opExtrude","SWEPT_FACE",FACE,{"disambiguationData":[OSD([sQuery(id+"F6.wireOp",EDGE,"E15")])]}),makeQuery(id+"F7.opExtrude","SWEPT_FACE",FACE,{"disambiguationData":[OSD([sQuery(id+"F6.wireOp",EDGE,"E16")])]}),makeQuery(id+"F7.opExtrude","SWEPT_FACE",FACE,{"disambiguationData":[OSD([sQuery(id+"F6.wireOp",EDGE,"E17")])]}),makeQuery(id+"F7.opExtrude","SWEPT_FACE",FACE,{"disambiguationData":[OSD([sQuery(id+"F6.wireOp",EDGE,"E18")])]}),makeQuery(id+"F7.opExtrude","SWEPT_FACE",FACE,{"disambiguationData":[OSD([sQuery(id+"F6.wireOp",EDGE,"E19")])]}),makeQuery(id+"F7.opExtrude","SWEPT_FACE",FACE,{"disambiguationData":[OSD([sQuery(id+"F6.wireOp",EDGE,"E20")])]}),makeQuery(id+"F7.opExtrude","SWEPT_FACE",FACE,{"disambiguationData":[OSD([sQuery(id+"F6.wireOp",EDGE,"E21")])]}),makeQuery(id+"F9.opExtrude","SWEPT_FACE",FACE,{"disambiguationData":[OSD([sQuery(id+"F8.wireOp",EDGE,"E22")])]}),makeQuery(id+"F9.opExtrude","SWEPT_FACE",FACE,{"disambiguationData":[OSD([sQuery(id+"F8.wireOp",EDGE,"E23")])]}),makeQuery(id+"F11.opExtrude","SWEPT_FACE",FACE,{"disambiguationData":[OSD([sQuery(id+"F10.wireOp",EDGE,"E24")])]}),makeQuery(id+"F11.opExtrude","SWEPT_FACE",FACE,{"disambiguationData":[OSD([sQuery(id+"F10.wireOp",EDGE,"E25")])]}),makeQuery(id+"F13.opExtrude","SWEPT_FACE",FACE,{"disambiguationData":[OSD([sQuery(id+"F12.wireOp",EDGE,"E26")])]}),makeQuery(id+"F13.opExtrude","SWEPT_FACE",FACE,{"disambiguationData":[OSD([sQuery(id+"F12.wireOp",EDGE,"E27")])]}),makeQuery(id+"F13.opExtrude","SWEPT_FACE",FACE,{"disambiguationData":[OSD([sQuery(id+"F12.wireOp",EDGE,"E28")])]}),makeQuery(id+"F13.opExtrude","SWEPT_FACE",FACE,{"disambiguationData":[OSD([sQuery(id+"F12.wireOp",EDGE,"E29")])]}),makeQuery(id+"F15.opExtrude","SWEPT_FACE",FACE,{"disambiguationData":[OSD([sQuery(id+"F14.wireOp",EDGE,"E30")])]}),makeQuery(id+"F15.opExtrude","SWEPT_FACE",FACE,{"disambiguationData":[OSD([sQuery(id+"F14.wireOp",EDGE,"E31")])]}),makeQuery(id+"F17.opExtrude","SWEPT_FACE",FACE,{"disambiguationData":[OSD([sQuery(id+"F16.wireOp",EDGE,"E32")])]}),makeQuery(id+"F17.opExtrude","SWEPT_FACE",FACE,{"disambiguationData":[OSD([sQuery(id+"F16.wireOp",EDGE,"E33")])]}),makeQuery(id+"F19.opExtrude","SWEPT_FACE",FACE,{"disambiguationData":[OSD([sQuery(id+"F18.wireOp",EDGE,"E34")])]}),makeQuery(id+"F19.opExtrude","SWEPT_FACE",FACE,{"disambiguationData":[OSD([sQuery(id+"F18.wireOp",EDGE,"E35")])]}),makeQuery(id+"F19.opExtrude","SWEPT_FACE",FACE,{"disambiguationData":[OSD([sQuery(id+"F18.wireOp",EDGE,"E36")])]}),makeQuery(id+"F21.opExtrude","SWEPT_FACE",FACE,{"disambiguationData":[OSD([sQuery(id+"F20.wireOp",EDGE,"E37")])]}),makeQuery(id+"F21.opExtrude","SWEPT_FACE",FACE,{"disambiguationData":[OSD([sQuery(id+"F20.wireOp",EDGE,"E39")])]})])],"derivedFrom":makeQuery(id+"F1.opRevolve","CAP_FACE",FACE,{"disambiguationData":[OSD([subQ0,sQuery(id+"F0.wireOp",EDGE,"E1")])],"isStart":false})});}
            var sketch = newSketch(context, id + "F34", { "sketchPlane" : qUnion([Q0])});
            skFitSpline(sketch, "E56", {"points": [v(-4.81, 35.16) * mm, v(-4.68, 32.87) * mm, v(-2.9, 31) * mm, v(-1.1, 32.78) * mm, v(-4.81, 35.16) * mm]});
            skSolve(sketch);
        }
        {
            var Q0;
            Q0 = qSketchRegion(id + "F34", true);
            extrude(context, id + "F35", {"entities" : qUnion([Q0]), "operationType" : NewBodyOperationType.ADD, "depth" : 2.1 * mm, "offsetDistance" : 25 * mm});
        }
        {
            var Q0;
            {var subQ0=sQuery(id+"F0.wireOp",EDGE,"E0");Q0=makeQuery(id+"F21.boolean.opBoolean","SPLIT",FACE,{"disambiguationData":[TD([makeQuery(id+"F1.opRevolve","SWEPT_FACE",FACE,{"disambiguationData":[OSD([subQ0])]}),makeQuery(id+"F5.opExtrude","SWEPT_FACE",FACE,{"disambiguationData":[OSD([sQuery(id+"F4.wireOp",EDGE,"E5")])]}),makeQuery(id+"F5.opExtrude","SWEPT_FACE",FACE,{"disambiguationData":[OSD([sQuery(id+"F4.wireOp",EDGE,"E6")])]}),makeQuery(id+"F5.opExtrude","SWEPT_FACE",FACE,{"disambiguationData":[OSD([sQuery(id+"F4.wireOp",EDGE,"E7")])]}),makeQuery(id+"F5.opExtrude","SWEPT_FACE",FACE,{"disambiguationData":[OSD([sQuery(id+"F4.wireOp",EDGE,"E8")])]}),makeQuery(id+"F5.opExtrude","SWEPT_FACE",FACE,{"disambiguationData":[OSD([sQuery(id+"F4.wireOp",EDGE,"E9")])]}),makeQuery(id+"F5.opExtrude","SWEPT_FACE",FACE,{"disambiguationData":[OSD([sQuery(id+"F4.wireOp",EDGE,"E10")])]}),makeQuery(id+"F5.opExtrude","SWEPT_FACE",FACE,{"disambiguationData":[OSD([sQuery(id+"F4.wireOp",EDGE,"E11")])]}),makeQuery(id+"F5.opExtrude","SWEPT_FACE",FACE,{"disambiguationData":[OSD([sQuery(id+"F4.wireOp",EDGE,"E12")])]}),makeQuery(id+"F7.opExtrude","SWEPT_FACE",FACE,{"disambiguationData":[OSD([sQuery(id+"F6.wireOp",EDGE,"E14")])]}),makeQuery(id+"F7.opExtrude","SWEPT_FACE",FACE,{"disambiguationData":[OSD([sQuery(id+"F6.wireOp",EDGE,"E15")])]}),makeQuery(id+"F7.opExtrude","SWEPT_FACE",FACE,{"disambiguationData":[OSD([sQuery(id+"F6.wireOp",EDGE,"E16")])]}),makeQuery(id+"F7.opExtrude","SWEPT_FACE",FACE,{"disambiguationData":[OSD([sQuery(id+"F6.wireOp",EDGE,"E17")])]}),makeQuery(id+"F7.opExtrude","SWEPT_FACE",FACE,{"disambiguationData":[OSD([sQuery(id+"F6.wireOp",EDGE,"E18")])]}),makeQuery(id+"F7.opExtrude","SWEPT_FACE",FACE,{"disambiguationData":[OSD([sQuery(id+"F6.wireOp",EDGE,"E19")])]}),makeQuery(id+"F7.opExtrude","SWEPT_FACE",FACE,{"disambiguationData":[OSD([sQuery(id+"F6.wireOp",EDGE,"E20")])]}),makeQuery(id+"F7.opExtrude","SWEPT_FACE",FACE,{"disambiguationData":[OSD([sQuery(id+"F6.wireOp",EDGE,"E21")])]}),makeQuery(id+"F9.opExtrude","SWEPT_FACE",FACE,{"disambiguationData":[OSD([sQuery(id+"F8.wireOp",EDGE,"E22")])]}),makeQuery(id+"F9.opExtrude","SWEPT_FACE",FACE,{"disambiguationData":[OSD([sQuery(id+"F8.wireOp",EDGE,"E23")])]}),makeQuery(id+"F11.opExtrude","SWEPT_FACE",FACE,{"disambiguationData":[OSD([sQuery(id+"F10.wireOp",EDGE,"E24")])]}),makeQuery(id+"F11.opExtrude","SWEPT_FACE",FACE,{"disambiguationData":[OSD([sQuery(id+"F10.wireOp",EDGE,"E25")])]}),makeQuery(id+"F13.opExtrude","SWEPT_FACE",FACE,{"disambiguationData":[OSD([sQuery(id+"F12.wireOp",EDGE,"E26")])]}),makeQuery(id+"F13.opExtrude","SWEPT_FACE",FACE,{"disambiguationData":[OSD([sQuery(id+"F12.wireOp",EDGE,"E27")])]}),makeQuery(id+"F13.opExtrude","SWEPT_FACE",FACE,{"disambiguationData":[OSD([sQuery(id+"F12.wireOp",EDGE,"E28")])]}),makeQuery(id+"F13.opExtrude","SWEPT_FACE",FACE,{"disambiguationData":[OSD([sQuery(id+"F12.wireOp",EDGE,"E29")])]}),makeQuery(id+"F15.opExtrude","SWEPT_FACE",FACE,{"disambiguationData":[OSD([sQuery(id+"F14.wireOp",EDGE,"E30")])]}),makeQuery(id+"F15.opExtrude","SWEPT_FACE",FACE,{"disambiguationData":[OSD([sQuery(id+"F14.wireOp",EDGE,"E31")])]}),makeQuery(id+"F17.opExtrude","SWEPT_FACE",FACE,{"disambiguationData":[OSD([sQuery(id+"F16.wireOp",EDGE,"E32")])]}),makeQuery(id+"F17.opExtrude","SWEPT_FACE",FACE,{"disambiguationData":[OSD([sQuery(id+"F16.wireOp",EDGE,"E33")])]}),makeQuery(id+"F19.opExtrude","SWEPT_FACE",FACE,{"disambiguationData":[OSD([sQuery(id+"F18.wireOp",EDGE,"E34")])]}),makeQuery(id+"F19.opExtrude","SWEPT_FACE",FACE,{"disambiguationData":[OSD([sQuery(id+"F18.wireOp",EDGE,"E35")])]}),makeQuery(id+"F19.opExtrude","SWEPT_FACE",FACE,{"disambiguationData":[OSD([sQuery(id+"F18.wireOp",EDGE,"E36")])]}),makeQuery(id+"F21.opExtrude","SWEPT_FACE",FACE,{"disambiguationData":[OSD([sQuery(id+"F20.wireOp",EDGE,"E37")])]}),makeQuery(id+"F21.opExtrude","SWEPT_FACE",FACE,{"disambiguationData":[OSD([sQuery(id+"F20.wireOp",EDGE,"E39")])]})])],"derivedFrom":makeQuery(id+"F1.opRevolve","CAP_FACE",FACE,{"disambiguationData":[OSD([subQ0,sQuery(id+"F0.wireOp",EDGE,"E1")])],"isStart":false})});}
            var sketch = newSketch(context, id + "F36", { "sketchPlane" : qUnion([Q0])});
            skFitSpline(sketch, "E57", {"points": [v(2.17, 35.58) * mm, v(0.55, 35) * mm, v(-0.58, 33.98) * mm, v(-0.68, 32.58) * mm, v(0.54, 32.02) * mm, v(2.17, 35.58) * mm]});
            skFitSpline(sketch, "E58", {"points": [v(3.51, 35.29) * mm, v(3.8, 33.66) * mm, v(4.42, 31.52) * mm, v(6.31, 32) * mm, v(6, 33.88) * mm, v(3.51, 35.29) * mm]});
            skFitSpline(sketch, "E59", {"points": [v(1.3, 28.31) * mm, v(0, 31.27) * mm, v(-1.45, 31.37) * mm, v(-2.67, 29.62) * mm, v(1.3, 28.31) * mm]});
            skFitSpline(sketch, "E60", {"points": [v(2.57, 28.67) * mm, v(1.81, 31.81) * mm, v(3, 33.06) * mm, v(3.72, 31.04) * mm, v(2.57, 28.67) * mm]});
            skSolve(sketch);
        }
        {
            var Q0;
            Q0 = qSketchRegion(id + "F36", true);
            extrude(context, id + "F37", {"entities" : qUnion([Q0]), "depth" : 2.1 * mm, "offsetDistance" : 25 * mm});
        }
        {
            var Q0;
            {var subQ0=sQuery(id+"F0.wireOp",EDGE,"E0");Q0=makeQuery(id+"F21.boolean.opBoolean","SPLIT",FACE,{"disambiguationData":[TD([makeQuery(id+"F1.opRevolve","SWEPT_FACE",FACE,{"disambiguationData":[OSD([subQ0])]}),makeQuery(id+"F5.opExtrude","SWEPT_FACE",FACE,{"disambiguationData":[OSD([sQuery(id+"F4.wireOp",EDGE,"E5")])]}),makeQuery(id+"F5.opExtrude","SWEPT_FACE",FACE,{"disambiguationData":[OSD([sQuery(id+"F4.wireOp",EDGE,"E6")])]}),makeQuery(id+"F5.opExtrude","SWEPT_FACE",FACE,{"disambiguationData":[OSD([sQuery(id+"F4.wireOp",EDGE,"E7")])]}),makeQuery(id+"F5.opExtrude","SWEPT_FACE",FACE,{"disambiguationData":[OSD([sQuery(id+"F4.wireOp",EDGE,"E8")])]}),makeQuery(id+"F5.opExtrude","SWEPT_FACE",FACE,{"disambiguationData":[OSD([sQuery(id+"F4.wireOp",EDGE,"E9")])]}),makeQuery(id+"F5.opExtrude","SWEPT_FACE",FACE,{"disambiguationData":[OSD([sQuery(id+"F4.wireOp",EDGE,"E10")])]}),makeQuery(id+"F5.opExtrude","SWEPT_FACE",FACE,{"disambiguationData":[OSD([sQuery(id+"F4.wireOp",EDGE,"E11")])]}),makeQuery(id+"F5.opExtrude","SWEPT_FACE",FACE,{"disambiguationData":[OSD([sQuery(id+"F4.wireOp",EDGE,"E12")])]}),makeQuery(id+"F7.opExtrude","SWEPT_FACE",FACE,{"disambiguationData":[OSD([sQuery(id+"F6.wireOp",EDGE,"E14")])]}),makeQuery(id+"F7.opExtrude","SWEPT_FACE",FACE,{"disambiguationData":[OSD([sQuery(id+"F6.wireOp",EDGE,"E15")])]}),makeQuery(id+"F7.opExtrude","SWEPT_FACE",FACE,{"disambiguationData":[OSD([sQuery(id+"F6.wireOp",EDGE,"E16")])]}),makeQuery(id+"F7.opExtrude","SWEPT_FACE",FACE,{"disambiguationData":[OSD([sQuery(id+"F6.wireOp",EDGE,"E17")])]}),makeQuery(id+"F7.opExtrude","SWEPT_FACE",FACE,{"disambiguationData":[OSD([sQuery(id+"F6.wireOp",EDGE,"E18")])]}),makeQuery(id+"F7.opExtrude","SWEPT_FACE",FACE,{"disambiguationData":[OSD([sQuery(id+"F6.wireOp",EDGE,"E19")])]}),makeQuery(id+"F7.opExtrude","SWEPT_FACE",FACE,{"disambiguationData":[OSD([sQuery(id+"F6.wireOp",EDGE,"E20")])]}),makeQuery(id+"F7.opExtrude","SWEPT_FACE",FACE,{"disambiguationData":[OSD([sQuery(id+"F6.wireOp",EDGE,"E21")])]}),makeQuery(id+"F9.opExtrude","SWEPT_FACE",FACE,{"disambiguationData":[OSD([sQuery(id+"F8.wireOp",EDGE,"E22")])]}),makeQuery(id+"F9.opExtrude","SWEPT_FACE",FACE,{"disambiguationData":[OSD([sQuery(id+"F8.wireOp",EDGE,"E23")])]}),makeQuery(id+"F11.opExtrude","SWEPT_FACE",FACE,{"disambiguationData":[OSD([sQuery(id+"F10.wireOp",EDGE,"E24")])]}),makeQuery(id+"F11.opExtrude","SWEPT_FACE",FACE,{"disambiguationData":[OSD([sQuery(id+"F10.wireOp",EDGE,"E25")])]}),makeQuery(id+"F13.opExtrude","SWEPT_FACE",FACE,{"disambiguationData":[OSD([sQuery(id+"F12.wireOp",EDGE,"E26")])]}),makeQuery(id+"F13.opExtrude","SWEPT_FACE",FACE,{"disambiguationData":[OSD([sQuery(id+"F12.wireOp",EDGE,"E27")])]}),makeQuery(id+"F13.opExtrude","SWEPT_FACE",FACE,{"disambiguationData":[OSD([sQuery(id+"F12.wireOp",EDGE,"E28")])]}),makeQuery(id+"F13.opExtrude","SWEPT_FACE",FACE,{"disambiguationData":[OSD([sQuery(id+"F12.wireOp",EDGE,"E29")])]}),makeQuery(id+"F15.opExtrude","SWEPT_FACE",FACE,{"disambiguationData":[OSD([sQuery(id+"F14.wireOp",EDGE,"E30")])]}),makeQuery(id+"F15.opExtrude","SWEPT_FACE",FACE,{"disambiguationData":[OSD([sQuery(id+"F14.wireOp",EDGE,"E31")])]}),makeQuery(id+"F17.opExtrude","SWEPT_FACE",FACE,{"disambiguationData":[OSD([sQuery(id+"F16.wireOp",EDGE,"E32")])]}),makeQuery(id+"F17.opExtrude","SWEPT_FACE",FACE,{"disambiguationData":[OSD([sQuery(id+"F16.wireOp",EDGE,"E33")])]}),makeQuery(id+"F19.opExtrude","SWEPT_FACE",FACE,{"disambiguationData":[OSD([sQuery(id+"F18.wireOp",EDGE,"E34")])]}),makeQuery(id+"F19.opExtrude","SWEPT_FACE",FACE,{"disambiguationData":[OSD([sQuery(id+"F18.wireOp",EDGE,"E35")])]}),makeQuery(id+"F19.opExtrude","SWEPT_FACE",FACE,{"disambiguationData":[OSD([sQuery(id+"F18.wireOp",EDGE,"E36")])]}),makeQuery(id+"F21.opExtrude","SWEPT_FACE",FACE,{"disambiguationData":[OSD([sQuery(id+"F20.wireOp",EDGE,"E37")])]}),makeQuery(id+"F21.opExtrude","SWEPT_FACE",FACE,{"disambiguationData":[OSD([sQuery(id+"F20.wireOp",EDGE,"E39")])]})])],"derivedFrom":makeQuery(id+"F1.opRevolve","CAP_FACE",FACE,{"disambiguationData":[OSD([subQ0,sQuery(id+"F0.wireOp",EDGE,"E1")])],"isStart":false})});}
            var sketch = newSketch(context, id + "F38", { "sketchPlane" : qUnion([Q0])});
            skFitSpline(sketch, "E61", {"points": [v(9.38, 39.14) * mm, v(7.6, 38.3) * mm, v(6.62, 36.9) * mm, v(7.67, 35.73) * mm, v(9.05, 36.74) * mm, v(9.38, 39.14) * mm]});
            skFitSpline(sketch, "E62", {"points": [v(10.7, 38.9) * mm, v(10.57, 37.57) * mm, v(10.9, 35.97) * mm, v(11.67, 35.4) * mm, v(12.74, 36.27) * mm, v(12.08, 37.93) * mm, v(10.7, 38.9) * mm]});
            skFitSpline(sketch, "E63", {"points": [v(7.52, 27.46) * mm, v(5.88, 28.36) * mm, v(5.04, 29.85) * mm, v(5.74, 31.1) * mm, v(7.45, 30.35) * mm, v(7.52, 27.46) * mm]});
            skFitSpline(sketch, "E64", {"points": [v(8.94, 27.87) * mm, v(8.73, 29) * mm, v(8.65, 31.62) * mm, v(10.38, 32.56) * mm, v(11.23, 30.7) * mm, v(8.94, 27.87) * mm]});
            skSolve(sketch);
        }
        {
            var Q0;
            Q0 = qSketchRegion(id + "F38", true);
            extrude(context, id + "F39", {"entities" : qUnion([Q0]), "depth" : 2.1 * mm, "offsetDistance" : 25 * mm});
        }
    });
